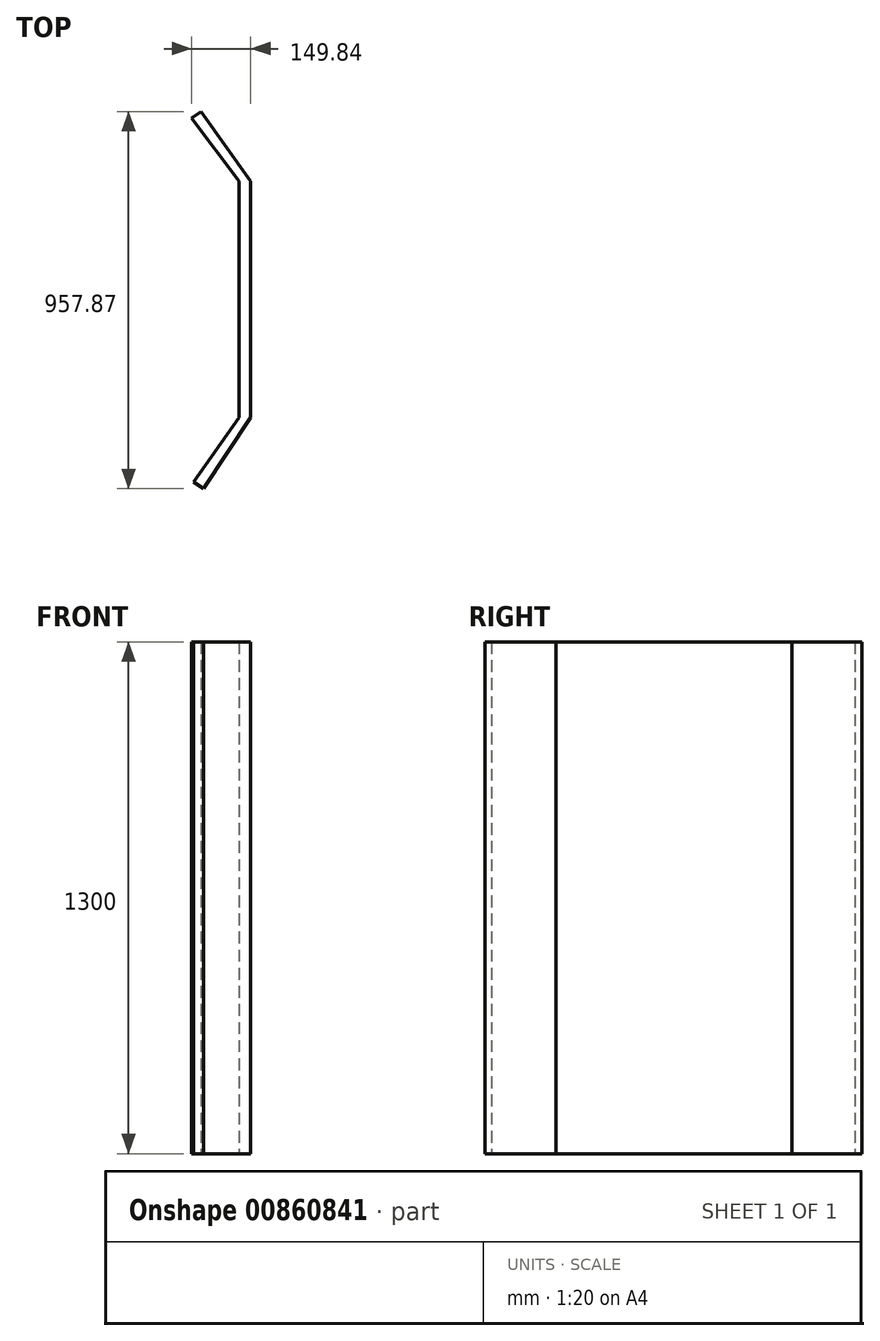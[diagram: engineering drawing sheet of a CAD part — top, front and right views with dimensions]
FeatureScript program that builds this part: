
annotation { "Feature Type Name" : "Feature", "Feature Type Description" : "" }
export const myFeature = defineFeature(function(context is Context, id is Id, definition is map)
    precondition{}
    {
        {
            var Q0;
            Q0=qCreatedBy(makeId("Top.planeOp"),FACE);
            var sketch = newSketch(context, id + "F0", { "sketchPlane" : qUnion([Q0])});
            skLineSegment(sketch, "E0.bottom", {"start": v(0.5, 177.32) * mm, "end": v(-29.5, 177.32) * mm});
            skLineSegment(sketch, "E0.top", {"start": v(0.5, -422.68) * mm, "end": v(-29.5, -422.68) * mm});
            skLineSegment(sketch, "E0.left", {"start": v(0.5, 177.32) * mm, "end": v(0.5, -422.68) * mm});
            skLineSegment(sketch, "E0.right", {"start": v(-29.5, 177.32) * mm, "end": v(-29.5, -422.68) * mm});
            skLineSegment(sketch, "E1", {"start": v(0.5, 177.32) * mm, "end": v(-124.83, 354.75) * mm});
            skLineSegment(sketch, "E2", {"start": v(-124.83, 354.75) * mm, "end": v(-149.33, 337.44) * mm});
            skLineSegment(sketch, "E3", {"start": v(-149.33, 337.44) * mm, "end": v(-29.5, 177.32) * mm});
            skLineSegment(sketch, "E4.MirrorCS", {"start": v(-149.33, -1182.8) * mm, "end": v(-29.5, -1022.68) * mm});
            skLineSegment(sketch, "E5.MirrorCS", {"start": v(0.5, -1022.68) * mm, "end": v(-124.83, -1200.11) * mm});
            skLineSegment(sketch, "E6", {"start": v(0.5, -422.68) * mm, "end": v(-119.18, -603.12) * mm});
            skLineSegment(sketch, "E7", {"start": v(-119.18, -603.12) * mm, "end": v(-144.18, -586.53) * mm});
            skLineSegment(sketch, "E8", {"start": v(-144.18, -586.53) * mm, "end": v(-29.5, -422.68) * mm});
            skSolve(sketch);
        }
        {
            var Q0;
            Q0=makeQuery(id+"F0.imprint","IMPRINT",FACE,{"disambiguationData":[TD([[makeQuery(id+"F0.imprint","IMPRINT",EDGE,{"derivedFrom":sQuery(id+"F0.wireOp",EDGE,"E0.bottom")}),1.0]])]});
            var Q1;
            Q1=makeQuery(id+"F0.imprint","IMPRINT",FACE,{"disambiguationData":[TD([[makeQuery(id+"F0.imprint","IMPRINT",EDGE,{"derivedFrom":sQuery(id+"F0.wireOp",EDGE,"E0.bottom")}),-1.0]])]});
            var Q2;
            Q2=makeQuery(id+"F0.imprint","IMPRINT",FACE,{"disambiguationData":[TD([[makeQuery(id+"F0.imprint","IMPRINT",EDGE,{"derivedFrom":sQuery(id+"F0.wireOp",EDGE,"E0.top")}),1.0]])]});
            extrude(context, id + "F1", {"entities" : qUnion([Q0, Q1, Q2]), "depth" : 1300 * mm, "offsetDistance" : 25 * mm});
        }
    });
